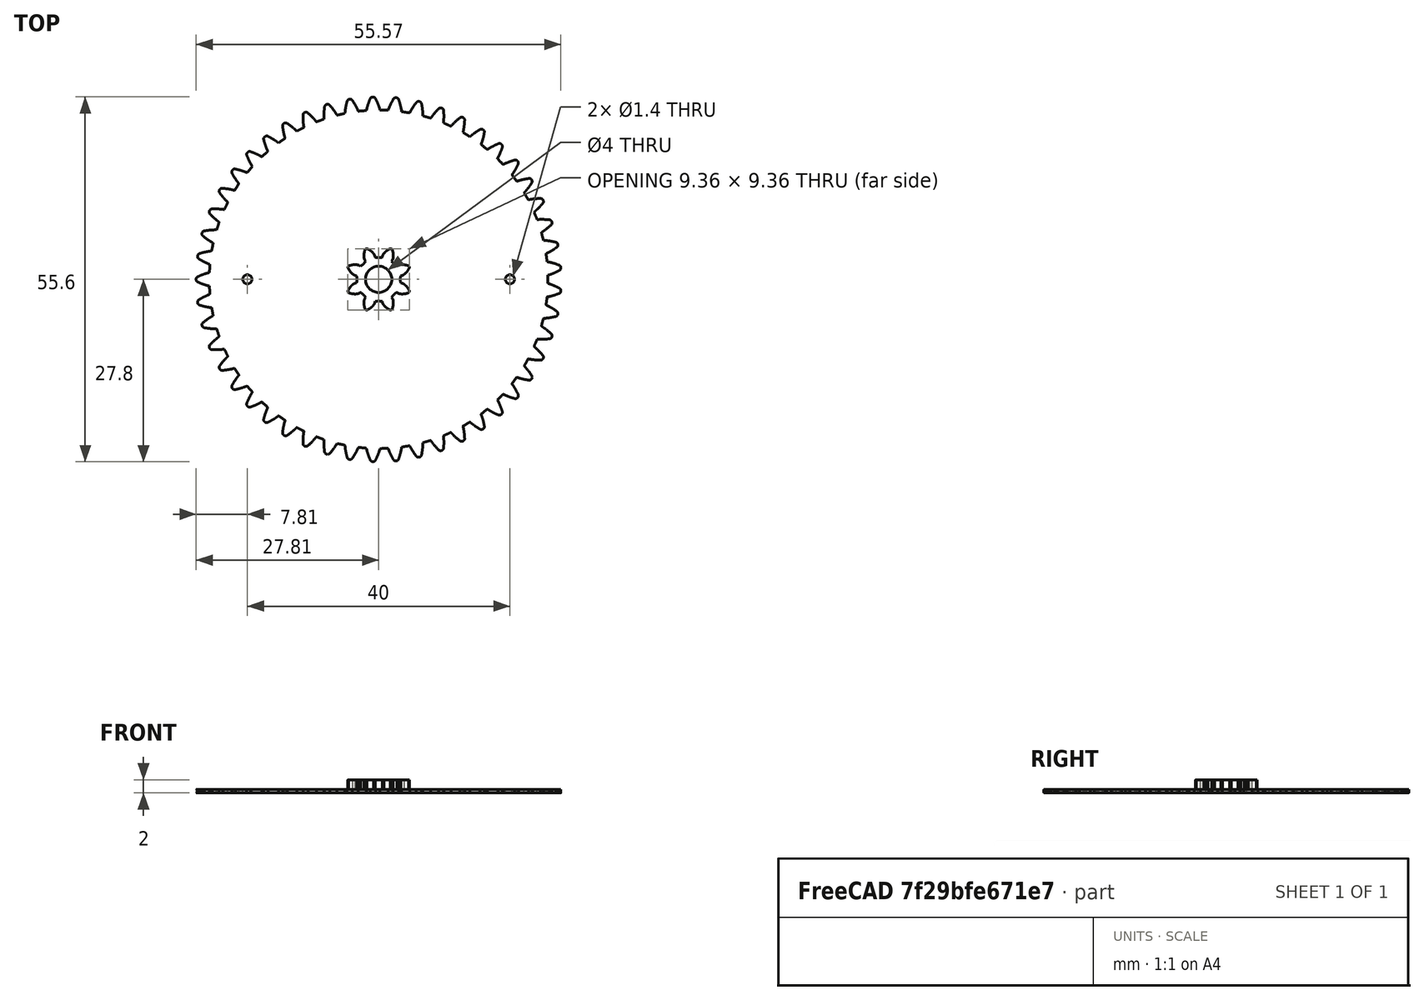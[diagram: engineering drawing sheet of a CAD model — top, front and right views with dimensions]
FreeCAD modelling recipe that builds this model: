
FCSTD DOCUMENT  (FreeCAD 0.18R4 (GitTag))
Label: Gear
License: All rights reserved
LicenseURL: http://en.wikipedia.org/wiki/All_rights_reserved
objects: Part::Cylinder×3, Part::Cut×3, Part::Part2DObjectPython×2, Part::Extrusion×2, Part::MultiFuse×1
note: 11 computed .brp shape members not serialized (recipe doc carries the construction recipe); baked Part::Feature solids carry a one-line shape summary decoded from their .brp

FEATURE [Part::Part2DObjectPython] InvoluteGear  # Draft 2D object (typed FeaturePython)
  ExternalGear = false
  HighPrecision = true
  Modules = 1.08
  NumberOfTeeth = 49
  PressureAngle = 20
FEATURE [Part::Part2DObjectPython] InvoluteGear001  # Draft 2D object (typed FeaturePython)
  ExternalGear = false
  HighPrecision = true
  Modules = 1
  NumberOfTeeth = 8
  PressureAngle = 26
FEATURE [Part::Extrusion] Extrude
  Base = -> InvoluteGear
  Dir = (0,0,1)
  DirMode = 2
  FaceMakerClass = Part::FaceMakerBullseye
  LengthFwd = 0.5
  LengthRev = 0
  Solid = true
  Symmetric = false
FEATURE [Part::Extrusion] Extrude001
  Base = -> InvoluteGear001
  Dir = (0,0,1)
  DirMode = 2
  FaceMakerClass = Part::FaceMakerBullseye
  LengthFwd = 2
  LengthRev = 0
  Solid = true
  Symmetric = false
FEATURE [Part::Cylinder] Cylinder  label="Цилиндр"
  Angle = 360
  AttacherType = Attacher::AttachEngine3D
  Height = 10
  Placement = pos=(0,0,-5) rot=(0,0,1;0rad)
  Radius = 2
FEATURE [Part::MultiFuse] Fusion
  Shapes = -> [Extrude,Extrude001]
FEATURE [Part::Cut] Cut
  Base = -> Fusion
  Tool = -> Cylinder
FEATURE [Part::Cylinder] Cylinder001  label="Цилиндр001"
  Angle = 360
  AttacherType = Attacher::AttachEngine3D
  Height = 10
  Placement = pos=(20,0,0) rot=(0,0,1;0rad)
  Radius = 0.7
FEATURE [Part::Cylinder] Cylinder002  label="Цилиндр002"
  Angle = 360
  AttacherType = Attacher::AttachEngine3D
  Height = 10
  Placement = pos=(-20,0,0) rot=(0,0,1;0rad)
  Radius = 0.7
FEATURE [Part::Cut] Cut001
  Base = -> Cut
  Tool = -> Cylinder001
FEATURE [Part::Cut] Cut002
  Base = -> Cut001
  Tool = -> Cylinder002
